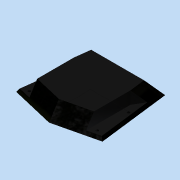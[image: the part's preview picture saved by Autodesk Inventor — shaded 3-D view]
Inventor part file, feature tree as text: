
AUTODESK INVENTOR PART (.ipt)
format: ipt  version: 2015 (Build 190159000, 159)  size: 225,280 bytes
history: native  units: in
note: dims shown in document units (in); Inventor stores cm internally (conversion verified against a paired STEP export)
features: sketch x7, other x4, extrude x4, plane x2, projected_geometry x2, loft x1, mirror x1
ambient origin geometry x8: Origin, YZ Plane, XZ Plane, XY Plane, X Axis, Y Axis, Z Axis, Center Point
bodies: Solid1 (feature_tree)
feature tree (21):
  other  "ElectronicsEnclosureBaseplate.ipt"
  sketch  "Sketch2"  dims[d2=0.0in d3=90.0deg d4=0.0in d5=90.0deg]
  plane  "Work Plane2"
  loft  "Loft1"
  extrude  "Extrusion1"  TaperAngle=0.0deg  [1 undecoded]
  extrude  "Extrusion2"  TaperAngle=0.0deg  [1 undecoded]
  mirror  "Mirror1"
  extrude  "Extrusion3"  TaperAngle=0.0deg  [1 undecoded]
  extrude  "Extrusion4"  Depth=1.0in
  other  "TaggingFeature1"
  sketch  "Sketch1"  dims[d0=0.3937in d1=1.25in]
  plane  "Work Plane1"
  sketch  "Sketch3"  dims[d6=1.125in d7=0.0in]
  sketch  "Sketch4"  dims[d8=1.0in d9=0.0in]
  projected_geometry  "Projected Loop1"
  sketch  "Sketch5"  dims[d10=0.75in d11=1.0in]
  sketch  "Sketch6"  dims[d12=0.0in]
  sketch  "Sketch7"  dims[d13=0.3125in d14=0.625in d15=1.0in d16=0.0in]
  projected_geometry  "Projected Loop2"
  other  "Solid1::ElectronicsEnclosureBaseplate.ipt"
  other  "Srf1"
note: 3 required parameter values undecoded (feature->parameter linkage not recoverable at this tier; creation-order binding heuristic only, values carry confidence <= 0.55)
